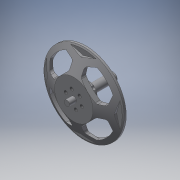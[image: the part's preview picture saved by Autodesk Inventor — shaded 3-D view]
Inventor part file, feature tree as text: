
AUTODESK INVENTOR PART (.ipt)
format: ipt  version: 2019.4 (Build 234330000, 330)  size: 351,232 bytes
history: native  units: mm
features: sketch x11, extrude x8, pattern_circular x3, fillet x2, hole x2, revolve x1, projected_geometry x1
ambient origin geometry x8: Origin, YZ Plane, XZ Plane, XY Plane, X Axis, Y Axis, Z Axis, Center Point
bodies: Solid1 (feature_tree)
feature tree (28):
  extrude  "Extrusion1"  Depth=9.0mm TaperAngle=0.0deg
  extrude  "Extrusion2"  Depth=28.0mm
  extrude  "Extrusion3"  Depth=7.5mm TaperAngle=0.0deg
  revolve  "Revolution1"  [1 undecoded]
  extrude  "Extrusion4"  Depth=40.0mm TaperAngle=360.0deg
  fillet  "Fillet1"  [1 undecoded]
  pattern_circular  "Circular Pattern1"  Count=4 Angle=360.0deg
  extrude  "Extrusion5"  Depth=4.2mm
  pattern_circular  "Circular Pattern2"  Count=4 Angle=360.0deg
  extrude  "Extrusion7"  Depth=2.0mm
  fillet  "Fillet2"  Radius=3.0mm
  hole  "Hole1"  [1 undecoded]
  pattern_circular  "Circular Pattern3"  [2 undecoded]
  extrude  "Extrusion6"  Depth=2.0mm TaperAngle=0.0deg
  extrude  "Extrusion8"  Depth=2.0mm
  hole  "Hole2"  [1 undecoded]
  sketch  "Sketch1"  dims[d0=58.6mm d1=9.0mm d2=0.0mm]
  sketch  "Sketch2"  dims[d3=3.7mm d4=28.0mm]
  sketch  "Sketch3"  dims[d5=3.7mm d6=0.0mm d7=7.5mm d8=0.0mm]
  projected_geometry  "Projected Loop1"
  sketch  "Sketch4"  dims[d9=90.0deg d10=8.6mm]
  sketch  "Sketch5"  dims[d11=4.3mm d12=40.0mm d14=360.0deg d16=45.0deg]
  sketch  "Sketch6"  dims[d18=16.5mm]
  sketch  "Sketch7"  dims[d19=7.5mm d20=0.0mm]
  sketch  "Sketch8"  dims[d21=2.0mm d22=40.0mm d23=360.0deg]
  sketch  "Sketch9"  dims[d25=4.2mm d26=4.2mm]
  sketch  "Sketch10"  dims[d27=7.0mm d28=0.0mm d29=40.0mm d30=360.0deg]
  sketch  "Sketch11"  dims[d32=45.0deg d33=6.0mm d34=3.0mm d35=2.459mm d36=10.0mm d37=4.34mm d38=2.0mm d39=1.22173mm d40=8.8mm d41=0.0mm d42=60.0mm d43=360.0deg d45=4.0mm d46=5.0mm d47=0.0mm d48=12.0mm d49=8.0mm d50=0.0mm d51=1.0mm d52=6.0mm d53=17.0mm d54=0.0mm d55=2.459mm d56=6.0mm d57=4.0mm d58=2.0mm d59=90.0deg d60=8.8mm d61=20.594885mm]
note: 6 required parameter values undecoded (feature->parameter linkage not recoverable at this tier; creation-order binding heuristic only, values carry confidence <= 0.55)